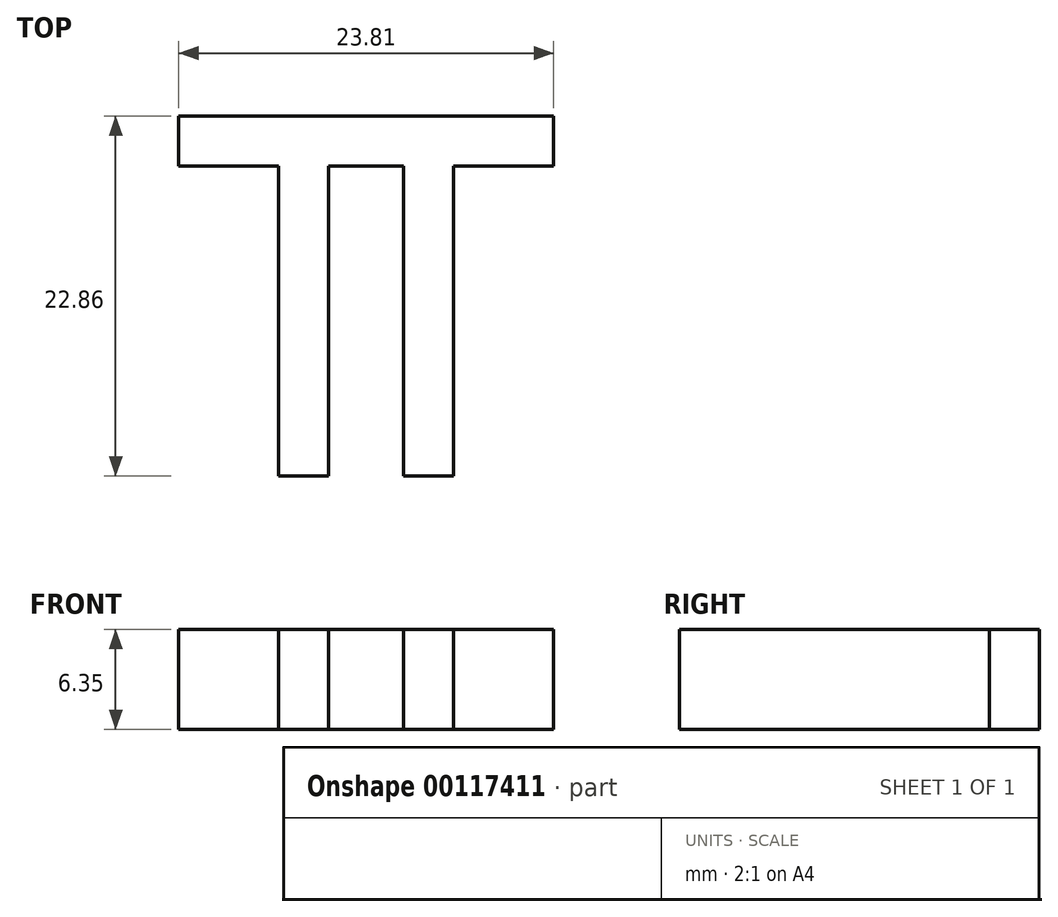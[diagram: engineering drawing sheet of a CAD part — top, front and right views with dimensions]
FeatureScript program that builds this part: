
annotation { "Feature Type Name" : "Feature", "Feature Type Description" : "" }
export const myFeature = defineFeature(function(context is Context, id is Id, definition is map)
    precondition{}
    {
        {
            var Q0;
            Q0=qCreatedBy(makeId("Front.planeOp"),FACE);
            var sketch = newSketch(context, id + "F0", { "sketchPlane" : qUnion([Q0])});
            skLineSegment(sketch, "E0.bottom", {"start": v(-6.95, 13.01) * mm, "end": v(-0.6, 13.01) * mm});
            skLineSegment(sketch, "E0.top", {"start": v(-6.95, 6.66) * mm, "end": v(-0.6, 6.66) * mm});
            skLineSegment(sketch, "E0.left", {"start": v(-6.95, 13.01) * mm, "end": v(-6.95, 6.66) * mm});
            skLineSegment(sketch, "E0.right", {"start": v(-0.6, 13.01) * mm, "end": v(-0.6, 6.66) * mm});
            skLineSegment(sketch, "E1.bottom", {"start": v(-0.6, 13.01) * mm, "end": v(2.58, 13.01) * mm});
            skLineSegment(sketch, "E1.top", {"start": v(-0.6, 6.66) * mm, "end": v(2.58, 6.66) * mm});
            skLineSegment(sketch, "E1.right", {"start": v(2.58, 13.01) * mm, "end": v(2.58, 6.66) * mm});
            skLineSegment(sketch, "E2.bottom", {"start": v(2.58, 13.01) * mm, "end": v(7.34, 13.01) * mm});
            skLineSegment(sketch, "E2.top", {"start": v(2.58, 6.66) * mm, "end": v(7.34, 6.66) * mm});
            skLineSegment(sketch, "E2.right", {"start": v(7.34, 13.01) * mm, "end": v(7.34, 6.66) * mm});
            skLineSegment(sketch, "E3.bottom", {"start": v(7.34, 13.01) * mm, "end": v(10.51, 13.01) * mm});
            skLineSegment(sketch, "E3.top", {"start": v(7.34, 6.66) * mm, "end": v(10.51, 6.66) * mm});
            skLineSegment(sketch, "E3.right", {"start": v(10.51, 13.01) * mm, "end": v(10.51, 6.66) * mm});
            skLineSegment(sketch, "E4.bottom", {"start": v(10.51, 13.01) * mm, "end": v(16.86, 13.01) * mm});
            skLineSegment(sketch, "E4.top", {"start": v(10.51, 6.66) * mm, "end": v(16.86, 6.66) * mm});
            skLineSegment(sketch, "E4.right", {"start": v(16.86, 13.01) * mm, "end": v(16.86, 6.66) * mm});
            skSolve(sketch);
        }
        {
            var Q0;
            Q0=makeQuery(id+"F0.imprint","IMPRINT",FACE,{"disambiguationData":[TD([[makeQuery(id+"F0.imprint","IMPRINT",EDGE,{"derivedFrom":sQuery(id+"F0.wireOp",EDGE,"E0.bottom")}),-1.0]])]});
            var Q1;
            Q1=makeQuery(id+"F0.imprint","IMPRINT",FACE,{"disambiguationData":[TD([[makeQuery(id+"F0.imprint","IMPRINT",EDGE,{"derivedFrom":sQuery(id+"F0.wireOp",EDGE,"E2.bottom")}),-1.0]])]});
            var Q2;
            Q2=makeQuery(id+"F0.imprint","IMPRINT",FACE,{"disambiguationData":[TD([[makeQuery(id+"F0.imprint","IMPRINT",EDGE,{"derivedFrom":sQuery(id+"F0.wireOp",EDGE,"E4.bottom")}),-1.0]])]});
            extrude(context, id + "F1", {"entities" : qUnion([Q0, Q1, Q2]), "depth" : 3.17 * mm});
        }
        {
            var Q0;
            Q0=makeQuery(id+"F0.imprint","IMPRINT",FACE,{"disambiguationData":[TD([[makeQuery(id+"F0.imprint","IMPRINT",EDGE,{"derivedFrom":sQuery(id+"F0.wireOp",EDGE,"E1.bottom")}),-1.0]])]});
            var Q1;
            Q1=makeQuery(id+"F0.imprint","IMPRINT",FACE,{"disambiguationData":[TD([[makeQuery(id+"F0.imprint","IMPRINT",EDGE,{"derivedFrom":sQuery(id+"F0.wireOp",EDGE,"E3.bottom")}),-1.0]])]});
            extrude(context, id + "F2", {"entities" : qUnion([Q0, Q1]), "operationType" : NewBodyOperationType.ADD, "depth" : 22.86 * mm});
        }
    });
